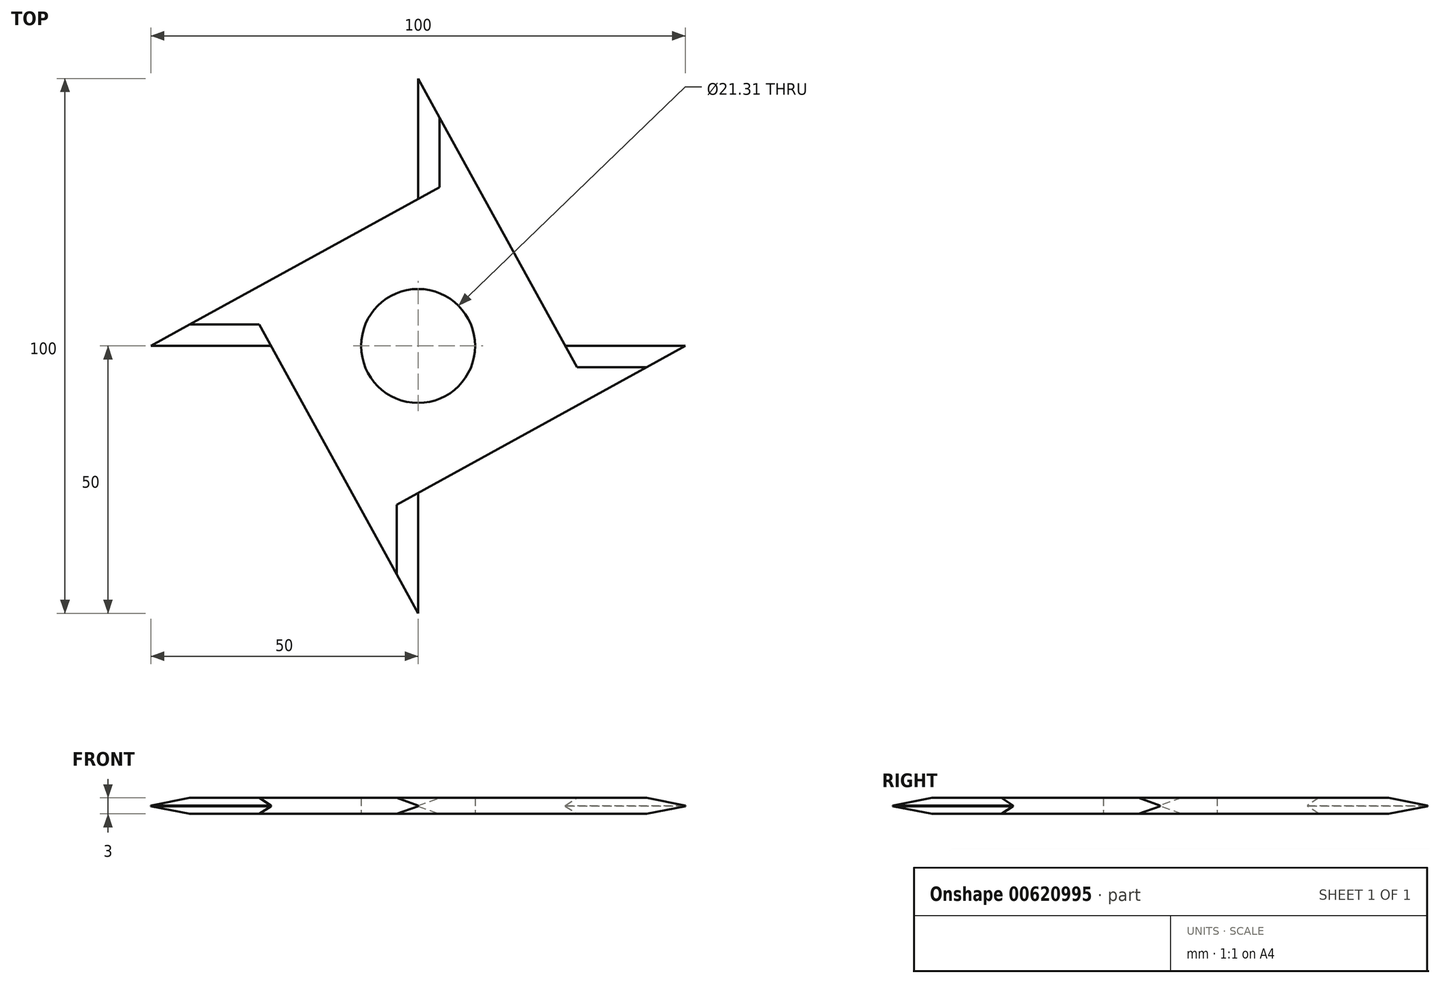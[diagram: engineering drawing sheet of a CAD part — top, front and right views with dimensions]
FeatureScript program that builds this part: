
annotation { "Feature Type Name" : "Feature", "Feature Type Description" : "" }
export const myFeature = defineFeature(function(context is Context, id is Id, definition is map)
    precondition{}
    {
        {
            var Q0;
            Q0=qCreatedBy(makeId("Top.planeOp"),FACE);
            var sketch = newSketch(context, id + "F0", { "sketchPlane" : qUnion([Q0])});
            skCircle(sketch, "E0", {"center": v(0, 0) * mm, "radius": 10.66 * mm});
            skLineSegment(sketch, "E1", {"start": v(0, 50) * mm, "end": v(27.5, 0) * mm});
            skLineSegment(sketch, "E2", {"start": v(0, 50) * mm, "end": v(0, 27.5) * mm});
            skCircle(sketch, "E3", {"center": v(0, 0) * mm, "radius": 50 * mm, "construction": true});
            skCircle(sketch, "E4", {"center": v(0, 0) * mm, "radius": 27.5 * mm, "construction": true});
            skLineSegment(sketch, "E5", {"start": v(27.5, 0) * mm, "end": v(50, 0) * mm});
            skLineSegment(sketch, "E6", {"start": v(50, 0) * mm, "end": v(0, -27.5) * mm});
            skLineSegment(sketch, "E7", {"start": v(0, -27.5) * mm, "end": v(0, -50) * mm});
            skLineSegment(sketch, "E8", {"start": v(0, -50) * mm, "end": v(-27.5, 0) * mm});
            skLineSegment(sketch, "E9", {"start": v(-27.5, 0) * mm, "end": v(-50, 0) * mm});
            skLineSegment(sketch, "E10", {"start": v(-50, 0) * mm, "end": v(0, 27.5) * mm});
            skSolve(sketch);
        }
        {
            var Q0;
            Q0 = qSketchRegion(id + "F0", true);
            extrude(context, id + "F1", {"entities" : qUnion([Q0]), "depth" : 3 * mm, "offsetDistance" : 25 * mm});
        }
        {
            var Q0;
            Q0=makeQuery(id+"F1.opExtrude","CAP_EDGE",EDGE,{"disambiguationData":[OSD([sQuery(id+"F0.wireOp",EDGE,"E9")])],"isStart":true});
            var Q1;
            Q1=makeQuery(id+"F1.opExtrude","CAP_EDGE",EDGE,{"disambiguationData":[OSD([sQuery(id+"F0.wireOp",EDGE,"E2")])],"isStart":true});
            var Q2;
            Q2=makeQuery(id+"F1.opExtrude","CAP_EDGE",EDGE,{"disambiguationData":[OSD([sQuery(id+"F0.wireOp",EDGE,"E5")])],"isStart":true});
            var Q3;
            Q3=makeQuery(id+"F1.opExtrude","CAP_EDGE",EDGE,{"disambiguationData":[OSD([sQuery(id+"F0.wireOp",EDGE,"E7")])],"isStart":true});
            chamfer(context, id + "F2", {"entities" : qUnion([Q0, Q1, Q2, Q3]), "chamferType" : ChamferType.TWO_OFFSETS, "width1" : 4 * mm, "oppositeDirection" : false, "width2" : 1.45 * mm});
        }
        {
            var Q0;
            Q0=makeQuery(id+"F1.opExtrude","CAP_EDGE",EDGE,{"disambiguationData":[OSD([sQuery(id+"F0.wireOp",EDGE,"E9")])],"isStart":false});
            var Q1;
            Q1=makeQuery(id+"F1.opExtrude","CAP_EDGE",EDGE,{"disambiguationData":[OSD([sQuery(id+"F0.wireOp",EDGE,"E5")])],"isStart":false});
            var Q2;
            Q2=makeQuery(id+"F1.opExtrude","CAP_EDGE",EDGE,{"disambiguationData":[OSD([sQuery(id+"F0.wireOp",EDGE,"E2")])],"isStart":false});
            var Q3;
            Q3=makeQuery(id+"F1.opExtrude","CAP_EDGE",EDGE,{"disambiguationData":[OSD([sQuery(id+"F0.wireOp",EDGE,"E7")])],"isStart":false});
            chamfer(context, id + "F3", {"entities" : qUnion([Q0, Q1, Q2, Q3]), "chamferType" : ChamferType.TWO_OFFSETS, "width1" : 1.45 * mm, "oppositeDirection" : false, "width2" : 4 * mm, "tangentPropagation" : true});
        }
    });
